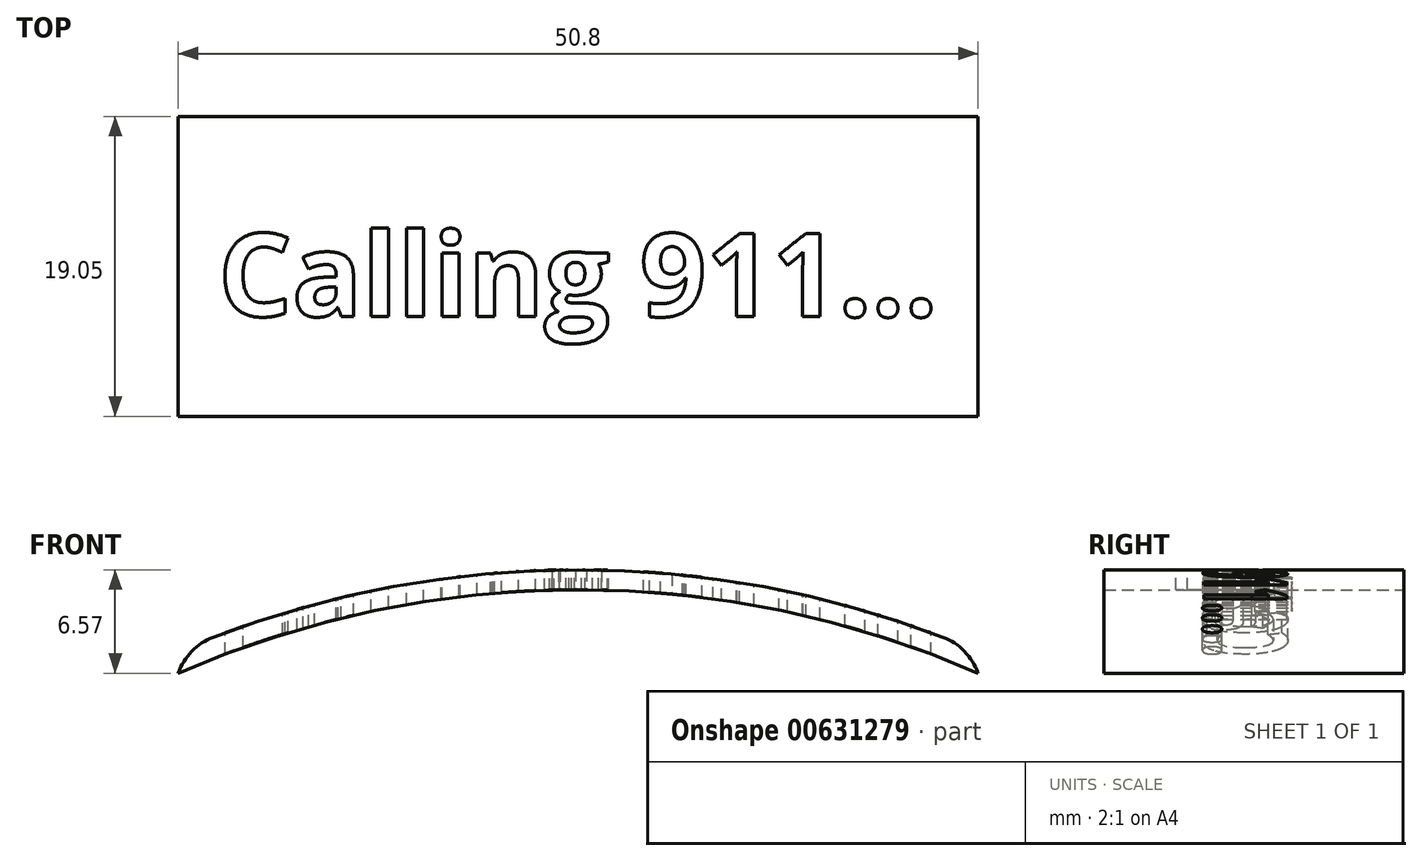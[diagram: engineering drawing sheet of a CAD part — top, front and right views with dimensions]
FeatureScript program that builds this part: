
annotation { "Feature Type Name" : "Feature", "Feature Type Description" : "" }
export const myFeature = defineFeature(function(context is Context, id is Id, definition is map)
    precondition{}
    {
        {
            var Q0;
            Q0=qCreatedBy(makeId("Front.planeOp"),FACE);
            var sketch = newSketch(context, id + "F0", { "sketchPlane" : qUnion([Q0])});
            skArc(sketch, "E0", {"start": v(25.4, 58.2) * mm, "mid": v(0, 63.5) * mm, "end": v(-25.4, 58.2) * mm});
            skArc(sketch, "E1", {"start": v(25.4, 59.58) * mm, "mid": v(0, 64.77) * mm, "end": v(-25.4, 59.58) * mm});
            skLineSegment(sketch, "E2", {"start": v(-25.4, 58.2) * mm, "end": v(-25.4, 59.58) * mm});
            skLineSegment(sketch, "E3", {"start": v(25.4, 58.2) * mm, "end": v(25.4, 59.58) * mm});
            skSolve(sketch);
        }
        {
            var Q0;
            Q0=makeQuery(id+"F0.imprint","IMPRINT",FACE,{"disambiguationData":[TD([[makeQuery(id+"F0.imprint","IMPRINT",EDGE,{"derivedFrom":sQuery(id+"F0.wireOp",EDGE,"E0")}),-1.0]])]});
            extrude(context, id + "F1", {"entities" : qUnion([Q0]), "depth" : 19.05 * mm, "offsetDistance" : 25.4 * mm});
        }
        {
            var Q0;
            Q0=qCreatedBy(makeId("Top.planeOp"),FACE);
            cPlane(context, id + "F2", {"entities" : qUnion([Q0]), "cplaneType" : CPlaneType.OFFSET, "offset" : 66.04 * mm, "width" : 152.4 * mm, "height" : 152.4 * mm});
        }
        {
            var Q0;
            Q0=qCreatedBy(id+"F2.planeOp",FACE);
            var sketch = newSketch(context, id + "F3", { "sketchPlane" : qUnion([Q0])});
            skText(sketch, "E4", { "text": "Calling 911...", "fontName": "OpenSans-Bold.ttf"});
            const initialGuessF3  = {"E4": [-0.02286, -0.0127, 1, 0, 0.0053]};
            skSetInitialGuess(sketch, initialGuessF3);
            skSolve(sketch);
        }
        {
            var Q0;
            Q0 = qSketchRegion(id + "F3", true);
            extrude(context, id + "F4", {"entities" : qUnion([Q0]), "operationType" : NewBodyOperationType.REMOVE, "oppositeDirection" : true, "depth" : 7.11 * mm, "offsetDistance" : 25.4 * mm});
        }
        {
            var Q0;
            Q0=makeQuery(id+"F1.opExtrude","SWEPT_EDGE",EDGE,{"disambiguationData":[OSD([sQuery(id+"F0.wireOp",EDGE,"E1"),sQuery(id+"F0.wireOp",EDGE,"E3")])]});
            var Q1;
            Q1=makeQuery(id+"F1.opExtrude","SWEPT_EDGE",EDGE,{"disambiguationData":[OSD([sQuery(id+"F0.wireOp",EDGE,"E1"),sQuery(id+"F0.wireOp",EDGE,"E2")])]});
            fillet(context, id + "F5", {"entities" : qUnion([Q0, Q1]), "radius" : 3.8 * mm, "tangentPropagation" : true, "allowEdgeOverflow" : false});
        }
    });
